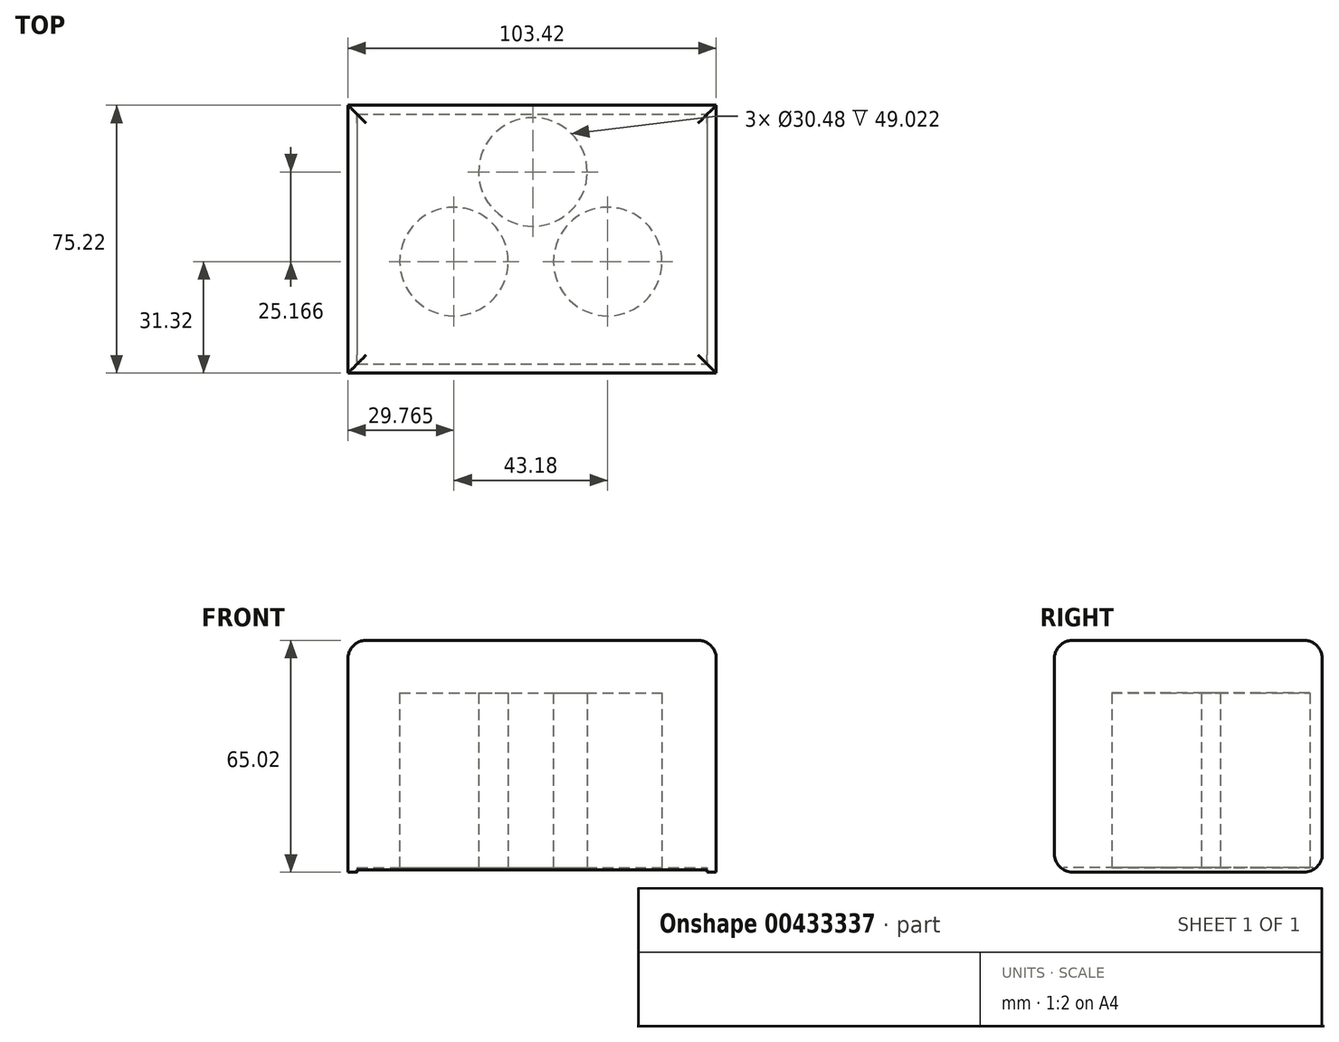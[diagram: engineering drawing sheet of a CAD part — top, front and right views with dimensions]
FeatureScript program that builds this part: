
annotation { "Feature Type Name" : "Feature", "Feature Type Description" : "" }
export const myFeature = defineFeature(function(context is Context, id is Id, definition is map)
    precondition{}
    {
        {
            var Q0;
            Q0=qCreatedBy(makeId("Top.planeOp"),FACE);
            var sketch = newSketch(context, id + "F0", { "sketchPlane" : qUnion([Q0])});
            skLineSegment(sketch, "E0.bottom", {"start": v(-44.8, 30.79) * mm, "end": v(58.62, 30.79) * mm});
            skLineSegment(sketch, "E0.top", {"start": v(-44.8, -44.43) * mm, "end": v(58.62, -44.43) * mm});
            skLineSegment(sketch, "E0.left", {"start": v(-44.8, 30.79) * mm, "end": v(-44.8, -44.43) * mm});
            skLineSegment(sketch, "E0.right", {"start": v(58.62, 30.79) * mm, "end": v(58.62, -44.43) * mm});
            skSolve(sketch);
        }
        {
            var Q0;
            Q0=makeQuery(id+"F0.imprint","IMPRINT",FACE,{"disambiguationData":[TD([[makeQuery(id+"F0.imprint","IMPRINT",EDGE,{"derivedFrom":sQuery(id+"F0.wireOp",EDGE,"E0.bottom")}),-1.0]])]});
            extrude(context, id + "F1", {"entities" : qUnion([Q0]), "depth" : 65.02 * mm});
        }
        {
            var Q0;
            Q0=makeQuery(id+"F1.opExtrude","CAP_FACE",FACE,{"disambiguationData":[OSD([sQuery(id+"F0.wireOp",EDGE,"E0.bottom"),sQuery(id+"F0.wireOp",EDGE,"E0.top"),sQuery(id+"F0.wireOp",EDGE,"E0.left"),sQuery(id+"F0.wireOp",EDGE,"E0.right")])],"isStart":true});
            shell(context, id + "F2", {"entities" : qUnion([Q0]), "thickness" : 2.54 * mm});
        }
        {
            var Q0;
            Q0=makeQuery(id+"F1.opExtrude","CAP_EDGE",EDGE,{"disambiguationData":[OSD([sQuery(id+"F0.wireOp",EDGE,"E0.top")])],"isStart":false});
            var Q1;
            Q1=makeQuery(id+"F1.opExtrude","CAP_EDGE",EDGE,{"disambiguationData":[OSD([sQuery(id+"F0.wireOp",EDGE,"E0.left")])],"isStart":false});
            var Q2;
            Q2=makeQuery(id+"F1.opExtrude","CAP_EDGE",EDGE,{"disambiguationData":[OSD([sQuery(id+"F0.wireOp",EDGE,"E0.bottom")])],"isStart":false});
            var Q3;
            Q3=makeQuery(id+"F1.opExtrude","CAP_EDGE",EDGE,{"disambiguationData":[OSD([sQuery(id+"F0.wireOp",EDGE,"E0.right")])],"isStart":false});
            var Q4;
            Q4=makeQuery(id+"F1.opExtrude","CAP_EDGE",EDGE,{"disambiguationData":[OSD([sQuery(id+"F0.wireOp",EDGE,"E0.bottom")])],"isStart":true});
            var Q5;
            Q5=makeQuery(id+"F1.opExtrude","CAP_EDGE",EDGE,{"disambiguationData":[OSD([sQuery(id+"F0.wireOp",EDGE,"E0.top")])],"isStart":true});
            fillet(context, id + "F3", {"entities" : qUnion([Q0, Q1, Q2, Q3, Q4, Q5]), "radius" : 5.08 * mm, "tangentPropagation" : true, "allowEdgeOverflow" : false});
        }
        {
            var Q0;
            Q0=makeQuery(id+"F2.opShell","OFFSET_FACE",FACE,{"disambiguationData":[OSD([sQuery(id+"F0.wireOp",EDGE,"E0.bottom"),sQuery(id+"F0.wireOp",EDGE,"E0.top"),sQuery(id+"F0.wireOp",EDGE,"E0.left"),sQuery(id+"F0.wireOp",EDGE,"E0.right")])]});
            var sketch = newSketch(context, id + "F4", { "sketchPlane" : qUnion([Q0])});
            skLineSegment(sketch, "E1", {"start": v(-10.85, 41.89) * mm, "end": v(-10.85, -28.25) * mm});
            skLineSegment(sketch, "E2", {"start": v(24.37, 41.89) * mm, "end": v(24.37, -25.9) * mm});
            skSolve(sketch);
        }
        {
            var Q0;
            Q0 = qSketchRegion(id + "F4", true);
            var Q1;
            {var subQ7=sQuery(id+"F4.wireOp",EDGE,"E1");Q1=makeQuery(id+"F4.imprint","IMPRINT",FACE,{"disambiguationData":[TD([[makeQuery(id+"F4.imprint","IMPRINT",EDGE,{"derivedFrom":subQ7}),1.0]])]});}
            var Q2;
            {var subQ0=sQuery(id+"F4.wireOp",EDGE,"E1");Q2=makeQuery(id+"F4.imprint","IMPRINT",FACE,{"disambiguationData":[TD([[makeQuery(id+"F4.imprint","IMPRINT",EDGE,{"derivedFrom":subQ0}),-1.0]])]});}
            extrude(context, id + "F5", {"entities" : qUnion([Q0, Q1, Q2]), "operationType" : NewBodyOperationType.ADD, "depth" : 61.2 * mm});
        }
        {
            var Q0;
            Q0=makeQuery(id+"F5.opExtrude","CAP_FACE",FACE,{"disambiguationData":[OSD([sQuery(id+"F0.wireOp",EDGE,"E0.bottom"),sQuery(id+"F0.wireOp",EDGE,"E0.top"),sQuery(id+"F0.wireOp",EDGE,"E0.left"),sQuery(id+"F0.wireOp",EDGE,"E0.right")])],"isStart":false});
            var sketch = newSketch(context, id + "F6", { "sketchPlane" : qUnion([Q0])});
            skCircle(sketch, "E3", {"center": v(-15.04, 13.1) * mm, "radius": 15.24 * mm});
            skCircle(sketch, "E4", {"center": v(28.14, 13.1) * mm, "radius": 15.24 * mm});
            skCircle(sketch, "E5", {"center": v(7.13, -12.06) * mm, "radius": 15.24 * mm});
            skSolve(sketch);
        }
        {
            var Q0;
            Q0=makeQuery(id+"F6.imprint","IMPRINT",FACE,{"disambiguationData":[TD([[makeQuery(id+"F6.imprint","IMPRINT",EDGE,{"derivedFrom":sQuery(id+"F6.wireOp",EDGE,"E3")}),1.0]])]});
            var Q1;
            Q1=makeQuery(id+"F6.imprint","IMPRINT",FACE,{"disambiguationData":[TD([[makeQuery(id+"F6.imprint","IMPRINT",EDGE,{"derivedFrom":sQuery(id+"F6.wireOp",EDGE,"E4")}),1.0]])]});
            var Q2;
            Q2=makeQuery(id+"F6.imprint","IMPRINT",FACE,{"disambiguationData":[TD([[makeQuery(id+"F6.imprint","IMPRINT",EDGE,{"derivedFrom":sQuery(id+"F6.wireOp",EDGE,"E5")}),1.0]])]});
            extrude(context, id + "F7", {"entities" : qUnion([Q0, Q1, Q2]), "operationType" : NewBodyOperationType.REMOVE, "oppositeDirection" : true, "depth" : 49.02 * mm});
        }
    });
